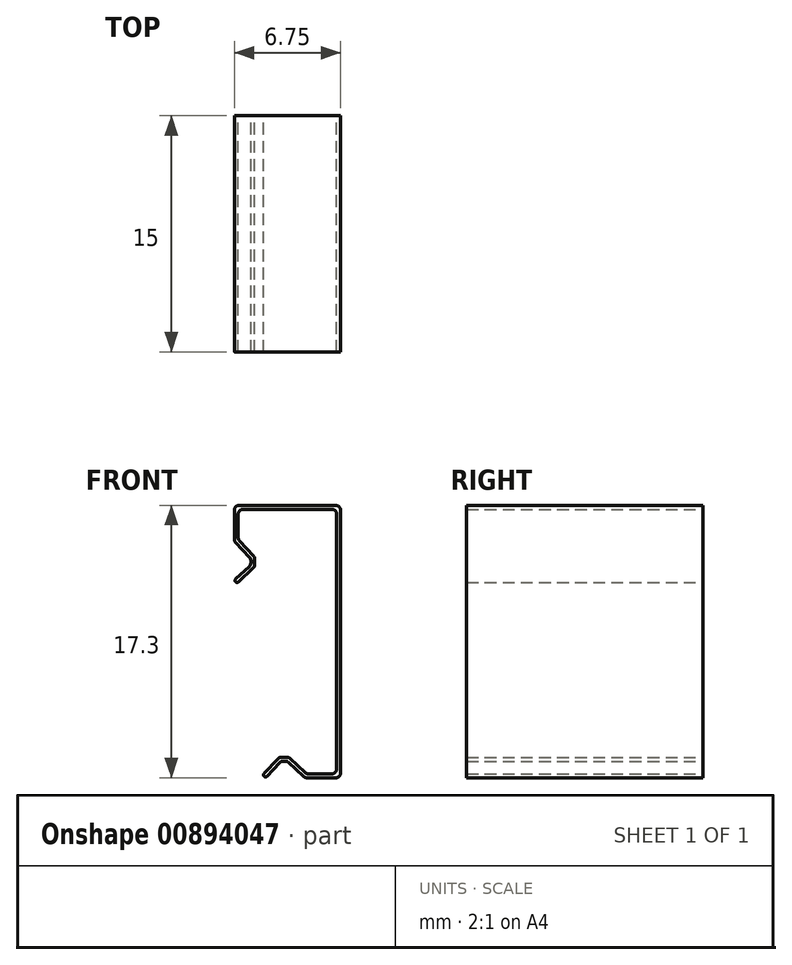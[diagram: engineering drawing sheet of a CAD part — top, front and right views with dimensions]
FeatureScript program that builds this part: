
annotation { "Feature Type Name" : "Feature", "Feature Type Description" : "" }
export const myFeature = defineFeature(function(context is Context, id is Id, definition is map)
    precondition{}
    {
        {
            var Q0;
            Q0=qCreatedBy(makeId("Front.planeOp"), FACE);
            var sketch = newSketch(context, id + "F0", { "sketchPlane" : qUnion([Q0]), "disableImprinting" : false});
            skLineSegment(sketch, "E0", {"start": v(-0.3, 0) * mm, "end": v(-6.45, 0) * mm});
            skLineSegment(sketch, "E1", {"start": v(-6.2, -0.25) * mm, "end": v(-0.55, -0.25) * mm});
            skLineSegment(sketch, "E2", {"start": v(-0.25, -0.55) * mm, "end": v(-0.25, -16.75) * mm});
            skLineSegment(sketch, "E3", {"start": v(0, -17) * mm, "end": v(0, -0.3) * mm});
            skPoint(sketch, "E4.start.orphan", {"position": v(-5.9, -15.8) * mm});
            skPoint(sketch, "E5.end.orphan", {"position": v(-5.49, -15.9) * mm});
            skLineSegment(sketch, "E6", {"start": v(-0.55, -17.05) * mm, "end": v(-2.05, -17.05) * mm});
            skLineSegment(sketch, "E7", {"start": v(-2.26, -16.97) * mm, "end": v(-3.2, -16.08) * mm});
            skLineSegment(sketch, "E8", {"start": v(-3.4, -16) * mm, "end": v(-3.76, -16) * mm});
            skLineSegment(sketch, "E9", {"start": v(-3.98, -16.1) * mm, "end": v(-4.86, -17.04) * mm});
            skLineSegment(sketch, "E10", {"start": v(-4.86, -17.21) * mm, "end": v(-4.86, -17.21) * mm});
            skLineSegment(sketch, "E11", {"start": v(-4.68, -17.2) * mm, "end": v(-3.87, -16.34) * mm});
            skLineSegment(sketch, "E12", {"start": v(-3.65, -16.25) * mm, "end": v(-3.5, -16.25) * mm});
            skLineSegment(sketch, "E13", {"start": v(-3.3, -16.33) * mm, "end": v(-2.35, -17.22) * mm});
            skLineSegment(sketch, "E14", {"start": v(-2.15, -17.3) * mm, "end": v(-0.3, -17.3) * mm});
            skPoint(sketch, "E15.visualSharp", {"position": v(-3.78, -16.25) * mm});
            skArc(sketch, "E15.filletArc", {"start": v(-3.65, -16.25) * mm, "mid": v(-3.77, -16.27) * mm, "end": v(-3.87, -16.34) * mm});
            skPoint(sketch, "E16.visualSharp", {"position": v(-3.38, -16.25) * mm});
            skArc(sketch, "E16.filletArc", {"start": v(-3.3, -16.33) * mm, "mid": v(-3.4, -16.27) * mm, "end": v(-3.5, -16.25) * mm});
            skPoint(sketch, "E17.visualSharp", {"position": v(-3.29, -16) * mm});
            skArc(sketch, "E17.filletArc", {"start": v(-3.2, -16.08) * mm, "mid": v(-3.3, -16.02) * mm, "end": v(-3.4, -16) * mm});
            skPoint(sketch, "E18.visualSharp", {"position": v(-3.89, -16) * mm});
            skArc(sketch, "E18.filletArc", {"start": v(-3.76, -16) * mm, "mid": v(-3.88, -16.02) * mm, "end": v(-3.98, -16.1) * mm});
            skPoint(sketch, "E19.visualSharp", {"position": v(-4.95, -17.13) * mm});
            skArc(sketch, "E19.filletArc", {"start": v(-4.86, -17.04) * mm, "mid": v(-4.9, -17.13) * mm, "end": v(-4.86, -17.21) * mm});
            skPoint(sketch, "E20.visualSharp", {"position": v(-4.77, -17.3) * mm});
            skArc(sketch, "E20.filletArc", {"start": v(-4.86, -17.21) * mm, "mid": v(-4.77, -17.25) * mm, "end": v(-4.68, -17.2) * mm});
            skPoint(sketch, "E21.start.orphan", {"position": v(-15.1, 0) * mm});
            skLineSegment(sketch, "E22", {"start": v(-6.75, -0.3) * mm, "end": v(-6.75, -2.15) * mm});
            skPoint(sketch, "E23.visualSharp", {"position": v(-10.4, -4.77) * mm});
            skPoint(sketch, "E24.visualSharp", {"position": v(-10.56, -6) * mm});
            skPoint(sketch, "E25.visualSharp", {"position": v(-10.22, -5.88) * mm});
            skPoint(sketch, "E26.visualSharp", {"position": v(-10.44, -4.26) * mm});
            skPoint(sketch, "E27.end.orphan", {"position": v(-11.83, -4.08) * mm});
            skLineSegment(sketch, "E28", {"start": v(-6.42, -2.26) * mm, "end": v(-5.53, -3.2) * mm});
            skLineSegment(sketch, "E29", {"start": v(-5.45, -3.4) * mm, "end": v(-5.45, -3.76) * mm});
            skLineSegment(sketch, "E30", {"start": v(-5.54, -3.98) * mm, "end": v(-6.49, -4.86) * mm});
            skLineSegment(sketch, "E31", {"start": v(-6.66, -4.86) * mm, "end": v(-6.66, -4.86) * mm});
            skLineSegment(sketch, "E32", {"start": v(-6.66, -4.68) * mm, "end": v(-5.8, -3.87) * mm});
            skLineSegment(sketch, "E33", {"start": v(-5.7, -3.65) * mm, "end": v(-5.7, -3.5) * mm});
            skLineSegment(sketch, "E34", {"start": v(-5.78, -3.3) * mm, "end": v(-6.67, -2.35) * mm});
            skPoint(sketch, "E35.visualSharp", {"position": v(-5.7, -3.78) * mm});
            skArc(sketch, "E35.filletArc", {"start": v(-5.8, -3.87) * mm, "mid": v(-5.72, -3.77) * mm, "end": v(-5.7, -3.65) * mm});
            skPoint(sketch, "E36.visualSharp", {"position": v(-5.7, -3.38) * mm});
            skArc(sketch, "E36.filletArc", {"start": v(-5.7, -3.5) * mm, "mid": v(-5.72, -3.4) * mm, "end": v(-5.78, -3.3) * mm});
            skPoint(sketch, "E37.visualSharp", {"position": v(-5.45, -3.89) * mm});
            skArc(sketch, "E37.filletArc", {"start": v(-5.54, -3.98) * mm, "mid": v(-5.47, -3.88) * mm, "end": v(-5.45, -3.76) * mm});
            skPoint(sketch, "E38.visualSharp", {"position": v(-5.45, -3.29) * mm});
            skArc(sketch, "E38.filletArc", {"start": v(-5.45, -3.4) * mm, "mid": v(-5.47, -3.3) * mm, "end": v(-5.53, -3.2) * mm});
            skPoint(sketch, "E39.visualSharp", {"position": v(-5.61, -2.3) * mm});
            skPoint(sketch, "E40.visualSharp", {"position": v(-6.75, -2.27) * mm});
            skPoint(sketch, "E41.visualSharp", {"position": v(-6.75, -4.77) * mm});
            skArc(sketch, "E41.filletArc", {"start": v(-6.66, -4.68) * mm, "mid": v(-6.7, -4.77) * mm, "end": v(-6.66, -4.86) * mm});
            skPoint(sketch, "E42.visualSharp", {"position": v(-6.58, -4.95) * mm});
            skArc(sketch, "E42.filletArc", {"start": v(-6.66, -4.86) * mm, "mid": v(-6.58, -4.9) * mm, "end": v(-6.49, -4.86) * mm});
            skPoint(sketch, "E43.visualSharp", {"position": v(-2.17, -17.05) * mm});
            skPoint(sketch, "E44.visualSharp", {"position": v(-2.27, -17.3) * mm});
            skPoint(sketch, "E45.visualSharp", {"position": v(-7.4, -2.93) * mm});
            skArc(sketch, "E45.filletArc", {"start": v(-6.2, -0.25) * mm, "mid": v(-6.41, -0.34) * mm, "end": v(-6.5, -0.55) * mm});
            skPoint(sketch, "E46.visualSharp", {"position": v(-6.75, 0) * mm});
            skArc(sketch, "E46.filletArc", {"start": v(-6.45, 0) * mm, "mid": v(-6.66, -0.09) * mm, "end": v(-6.75, -0.3) * mm});
            skPoint(sketch, "E47.visualSharp", {"position": v(-0.25, -0.25) * mm});
            skPoint(sketch, "E48.visualSharp", {"position": v(0, 0) * mm});
            skPoint(sketch, "E49.visualSharp", {"position": v(0, -17.3) * mm});
            skArc(sketch, "E49.filletArc", {"start": v(-0.3, -17.3) * mm, "mid": v(-0.09, -17.21) * mm, "end": v(0, -17) * mm});
            skPoint(sketch, "E50.visualSharp", {"position": v(-0.25, -17.05) * mm});
            skArc(sketch, "E50.filletArc", {"start": v(-0.55, -17.05) * mm, "mid": v(-0.34, -16.96) * mm, "end": v(-0.25, -16.75) * mm});
            skLineSegment(sketch, "E51", {"start": v(-6.5, -2.05) * mm, "end": v(-6.5, -0.55) * mm});
            skPoint(sketch, "E52.visualSharp", {"position": v(-6.5, -2.17) * mm});
            skArc(sketch, "E52.filletArc", {"start": v(-6.5, -2.05) * mm, "mid": v(-6.48, -2.16) * mm, "end": v(-6.42, -2.26) * mm});
            skArc(sketch, "E53.filletArc", {"start": v(-6.75, -2.15) * mm, "mid": v(-6.73, -2.26) * mm, "end": v(-6.67, -2.35) * mm});
            skArc(sketch, "E54.filletArc", {"start": v(-0.25, -0.55) * mm, "mid": v(-0.34, -0.34) * mm, "end": v(-0.55, -0.25) * mm});
            skArc(sketch, "E55.filletArc", {"start": v(0, -0.3) * mm, "mid": v(-0.09, -0.09) * mm, "end": v(-0.3, 0) * mm});
            skArc(sketch, "E56.filletArc", {"start": v(-2.26, -16.97) * mm, "mid": v(-2.16, -17.03) * mm, "end": v(-2.05, -17.05) * mm});
            skArc(sketch, "E57.filletArc", {"start": v(-2.35, -17.22) * mm, "mid": v(-2.26, -17.28) * mm, "end": v(-2.15, -17.3) * mm});
            skSolve(sketch);
        }
        {
            var Q0;
            Q0 = qSketchRegion(id + "F0", true);
            extrude(context, id + "F1", {"entities" : qUnion([Q0]), "depth" : 15 * mm, "offsetDistance" : 25 * mm});
        }
    });
